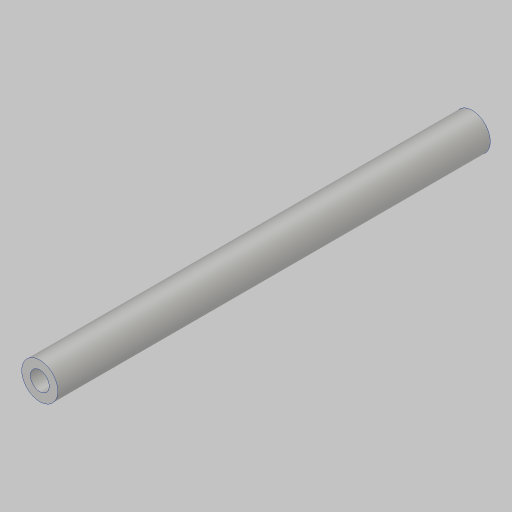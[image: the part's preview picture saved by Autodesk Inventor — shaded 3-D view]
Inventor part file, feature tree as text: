
AUTODESK INVENTOR PART (.ipt)
format: ipt  version: 2023.5 (Build 275446000, 446)  size: 104,448 bytes
history: native  units: in
note: dims shown in document units (in); Inventor stores cm internally (conversion verified against a paired STEP export)
features: extrude x1, hole x1
ambient origin geometry x8: Origin, YZ Plane, XZ Plane, XY Plane, X Axis, Y Axis, Z Axis, Center Point
bodies: Solid1 (feature_tree)
feature tree (2):
  extrude  "Extrusion1"  Depth=4.5in
  hole  "Hole1"  [1 undecoded]
note: 1 required parameter value undecoded (feature->parameter linkage not recoverable at this tier; creation-order binding heuristic only, values carry confidence <= 0.55)
